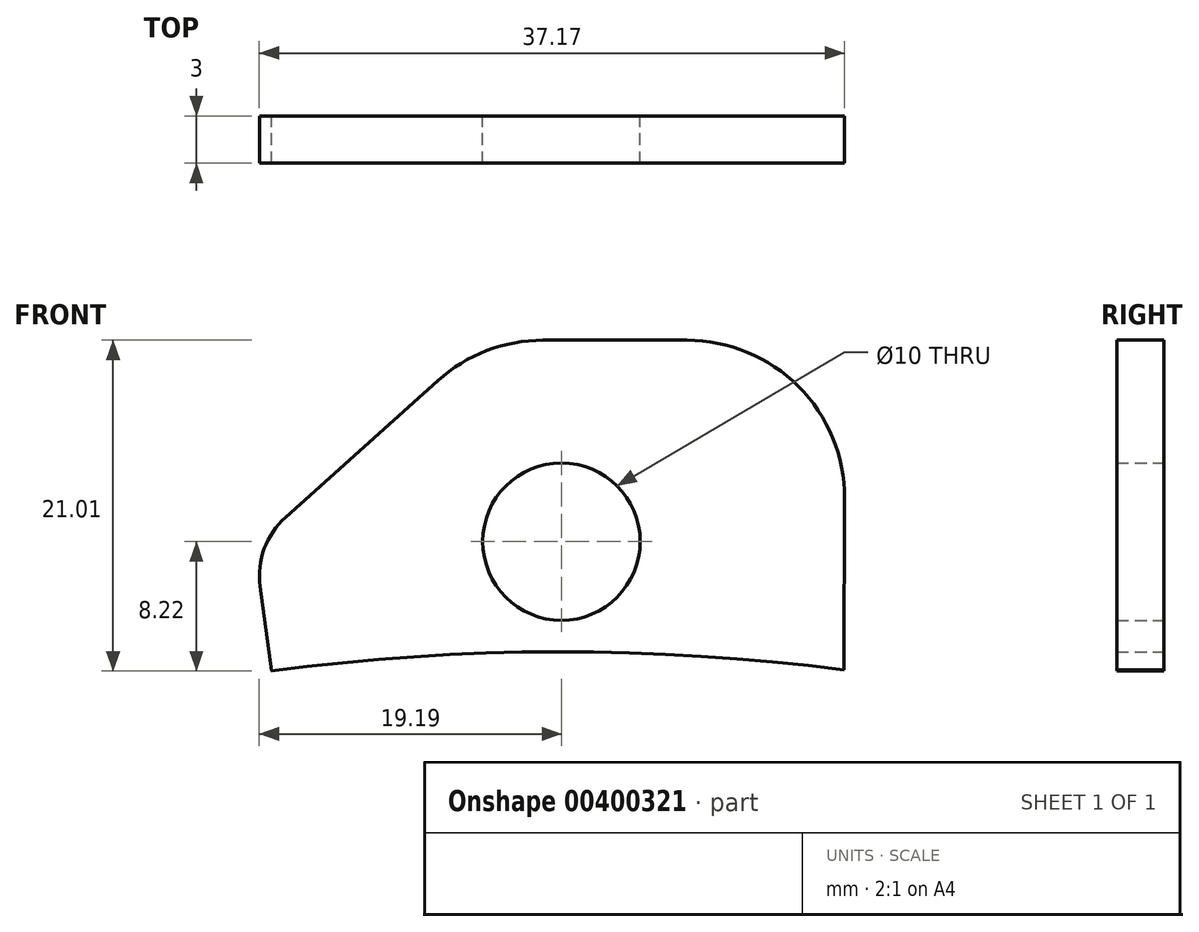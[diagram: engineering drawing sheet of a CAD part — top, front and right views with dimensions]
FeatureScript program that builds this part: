
annotation { "Feature Type Name" : "Feature", "Feature Type Description" : "" }
export const myFeature = defineFeature(function(context is Context, id is Id, definition is map)
    precondition{}
    {
        {
            var Q0;
            Q0=qCreatedBy(makeId("Front.planeOp"),FACE);
            var sketch = newSketch(context, id + "F0", { "sketchPlane" : qUnion([Q0])});
            skArc(sketch, "E0", {"start": v(17.95, 138.84) * mm, "mid": v(-0.24, 140) * mm, "end": v(-18.43, 138.78) * mm});
            skLineSegment(sketch, "E1", {"start": v(0, 0) * mm, "end": v(0, 164.8) * mm, "construction": true});
            skCircle(sketch, "E2", {"center": v(0, 147) * mm, "radius": 5 * mm});
            skLineSegment(sketch, "E3", {"start": v(-18.43, 138.78) * mm, "end": v(-19.49, 146.78) * mm});
            skLineSegment(sketch, "E4", {"start": v(0, 159.79) * mm, "end": v(18, 159.79) * mm});
            skLineSegment(sketch, "E5", {"start": v(0, 159.79) * mm, "end": v(-5, 159.79) * mm});
            skLineSegment(sketch, "E6", {"start": v(-5, 159.79) * mm, "end": v(-19.49, 146.78) * mm});
            skLineSegment(sketch, "E7", {"start": v(18, 159.79) * mm, "end": v(17.95, 138.84) * mm});
            skSolve(sketch);
        }
        {
            var Q0;
            Q0=makeQuery(id+"F0.imprint","IMPRINT",FACE,{"disambiguationData":[TD([[makeQuery(id+"F0.imprint","IMPRINT",EDGE,{"derivedFrom":sQuery(id+"F0.wireOp",EDGE,"E0")}),-1.0]])]});
            extrude(context, id + "F1", {"entities" : qUnion([Q0]), "depth" : 3 * mm, "offsetDistance" : 25 * mm});
        }
        {
            var Q0;
            Q0=makeQuery(id+"F1.opExtrude","SWEPT_EDGE",EDGE,{"disambiguationData":[OSD([sQuery(id+"F0.wireOp",EDGE,"E4"),sQuery(id+"F0.wireOp",EDGE,"E7")])]});
            var Q1;
            Q1=makeQuery(id+"F1.opExtrude","SWEPT_EDGE",EDGE,{"disambiguationData":[OSD([sQuery(id+"F0.wireOp",EDGE,"E5"),sQuery(id+"F0.wireOp",EDGE,"E6")])]});
            fillet(context, id + "F2", {"entities" : qUnion([Q0, Q1]), "radius" : 10 * mm, "tangentPropagation" : true, "allowEdgeOverflow" : false});
        }
        {
            var Q0;
            Q0=makeQuery(id+"F1.opExtrude","SWEPT_EDGE",EDGE,{"disambiguationData":[OSD([sQuery(id+"F0.wireOp",EDGE,"E3"),sQuery(id+"F0.wireOp",EDGE,"E6")])]});
            fillet(context, id + "F3", {"entities" : qUnion([Q0]), "radius" : 5 * mm, "tangentPropagation" : true, "allowEdgeOverflow" : false});
        }
    });
